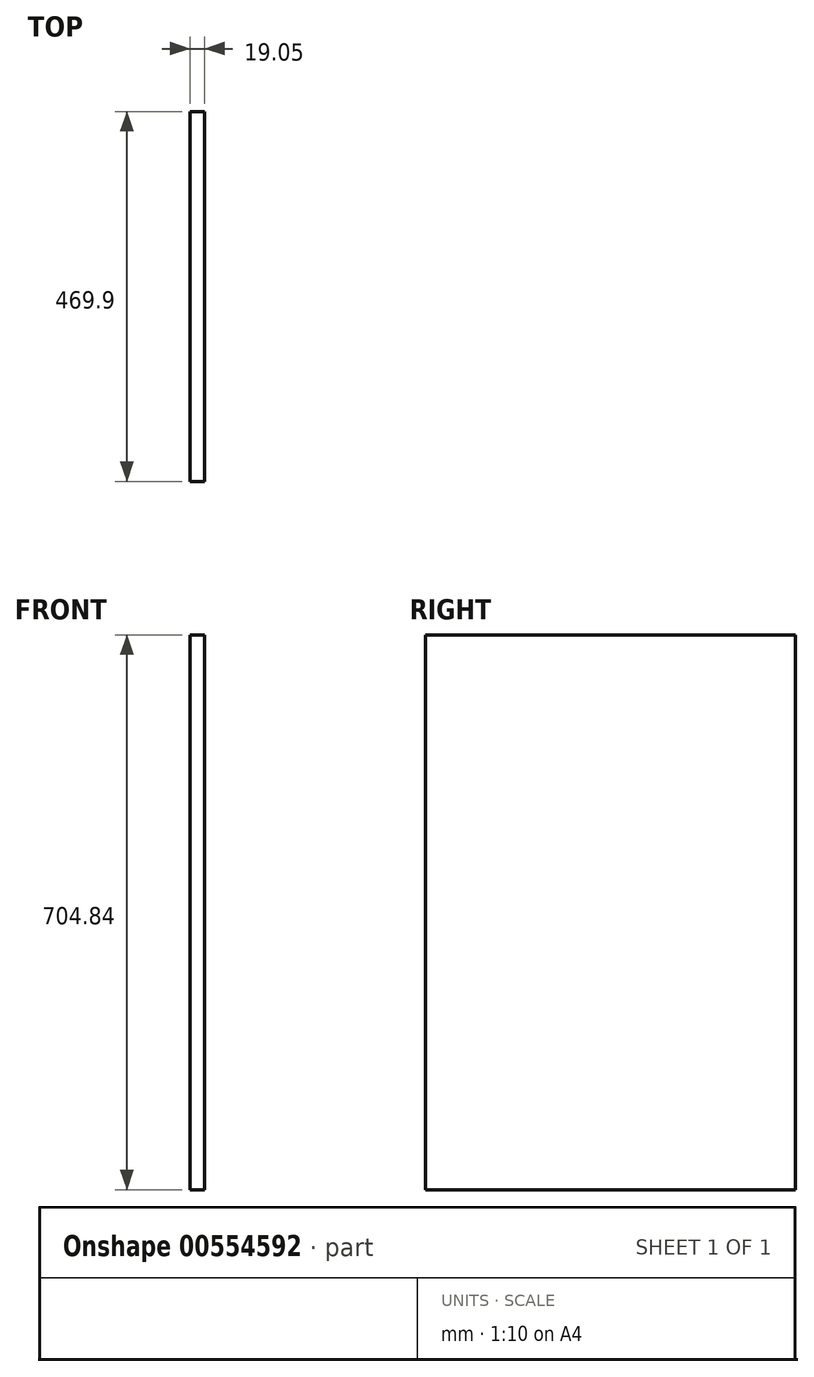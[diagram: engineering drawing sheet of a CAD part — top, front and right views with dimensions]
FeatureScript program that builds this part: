
annotation { "Feature Type Name" : "Feature", "Feature Type Description" : "" }
export const myFeature = defineFeature(function(context is Context, id is Id, definition is map)
    precondition{}
    {
        {
            var Q0;
            Q0=qCreatedBy(makeId("Right.planeOp"),FACE);
            var sketch = newSketch(context, id + "F0", { "sketchPlane" : qUnion([Q0])});
            skLineSegment(sketch, "E0.bottom", {"start": v(234.95, 517.52) * mm, "end": v(-234.95, 517.52) * mm});
            skLineSegment(sketch, "E0.top", {"start": v(234.95, -517.52) * mm, "end": v(-234.95, -517.52) * mm});
            skLineSegment(sketch, "E0.left", {"start": v(234.95, 517.52) * mm, "end": v(234.95, -517.52) * mm});
            skLineSegment(sketch, "E0.right", {"start": v(-234.95, 517.52) * mm, "end": v(-234.95, -517.52) * mm});
            skPoint(sketch, "E0.middle", {"position": v(0, 0) * mm});
            skSolve(sketch);
        }
        {
            var Q0;
            Q0=makeQuery(id+"F0.imprint","IMPRINT",FACE,{"disambiguationData":[TD([[makeQuery(id+"F0.imprint","IMPRINT",EDGE,{"derivedFrom":sQuery(id+"F0.wireOp",EDGE,"E0.bottom")}),1.0]])]});
            extrude(context, id + "F1", {"entities" : qUnion([Q0]), "depth" : 19.05 * mm, "offsetDistance" : 25.4 * mm});
        }
        {
            var Q0;
            Q0=makeQuery(id+"F1.opExtrude","SWEPT_FACE",FACE,{"disambiguationData":[OSD([sQuery(id+"F0.wireOp",EDGE,"E0.top")])]});
            extrude(context, id + "F2", {"entities" : qUnion([Q0]), "operationType" : NewBodyOperationType.REMOVE, "oppositeDirection" : true, "depth" : 330.2 * mm, "offsetDistance" : 25.4 * mm});
        }
    });
